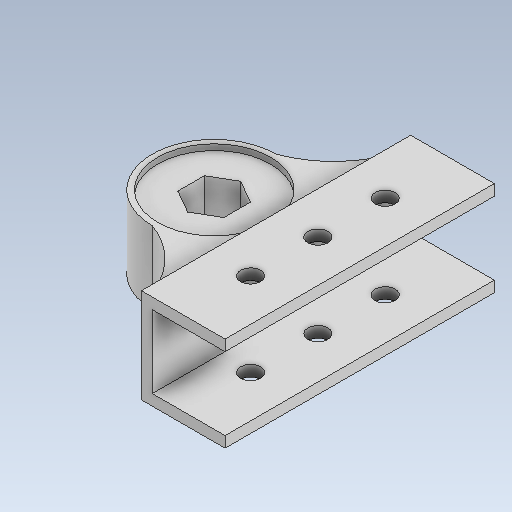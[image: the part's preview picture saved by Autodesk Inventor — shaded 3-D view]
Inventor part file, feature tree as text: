
AUTODESK INVENTOR PART (.ipt)
format: ipt  version: 2023 (Build 270158000, 158)  size: 172,544 bytes
history: native  units: in
note: dims shown in document units (in); Inventor stores cm internally (conversion verified against a paired STEP export)
features: sketch x11, other x3
ambient origin geometry x8: Origin, YZ Plane, XZ Plane, XY Plane, X Axis, Y Axis, Z Axis, Center Point
bodies: Solid1 (feature_tree)
feature tree (14):
  other  "CH-1-01-BearingBracket.ipt"
  other  "Solid1::CH-1-01-BearingBracket.ipt"
  other  "TaggingFeature1"
  sketch  "Sketch1"  dims[d0=0.3937in]
  sketch  "Sketch2"
  sketch  "Sketch4"
  sketch  "Sketch5"
  sketch  "Sketch7"
  sketch  "Sketch9"
  sketch  "Sketch11"
  sketch  "Sketch12"
  sketch  "Sketch13"
  sketch  "Sketch14"
  sketch  "Sketch15"
